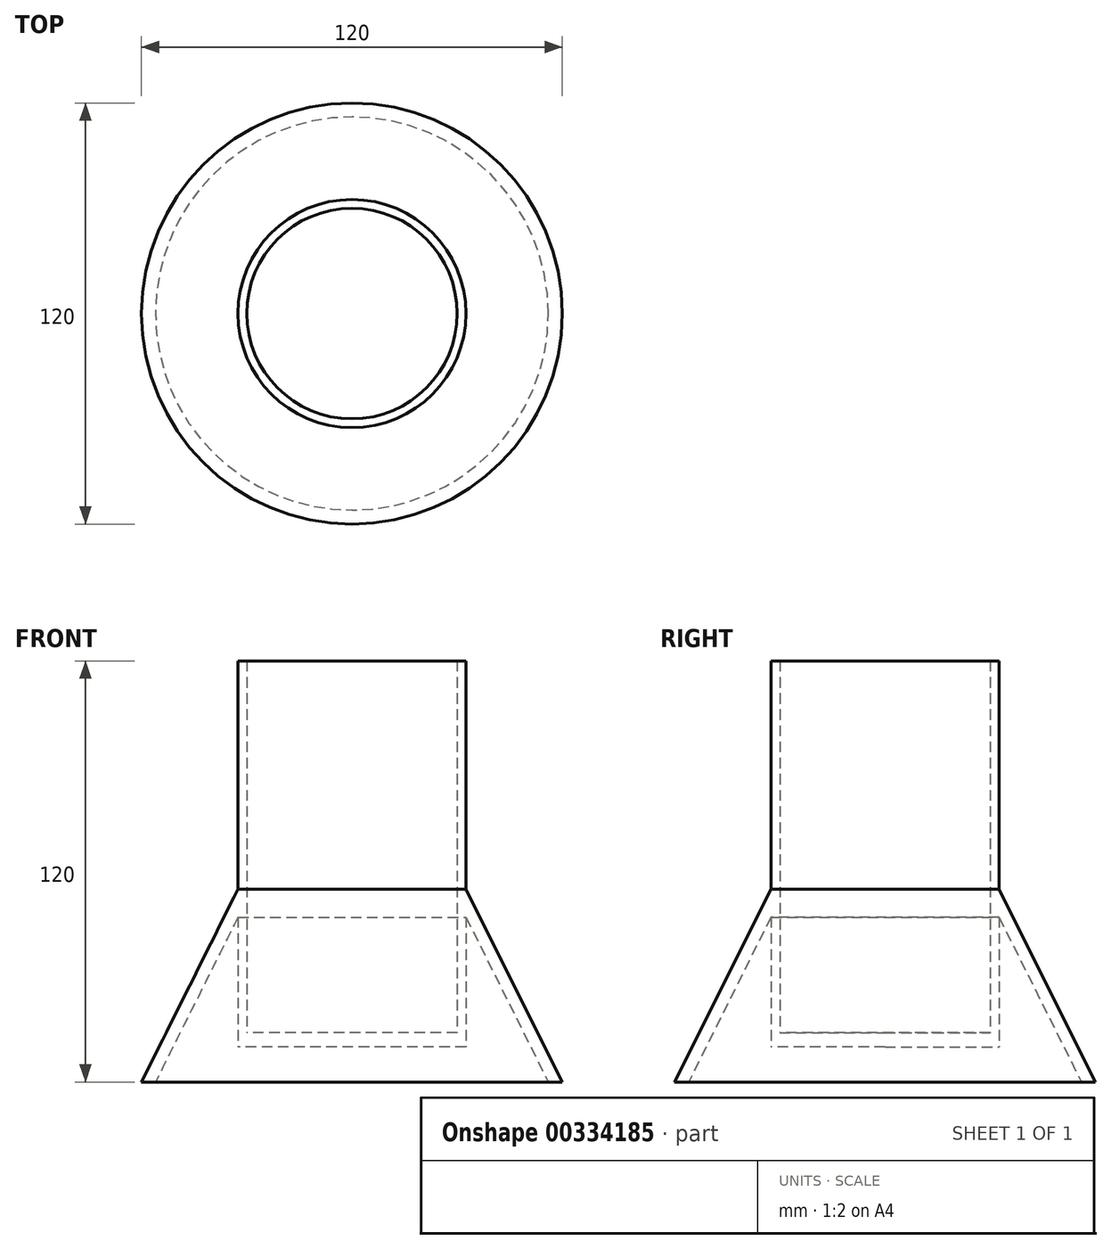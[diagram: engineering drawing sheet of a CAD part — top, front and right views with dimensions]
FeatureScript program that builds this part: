
annotation { "Feature Type Name" : "Feature", "Feature Type Description" : "" }
export const myFeature = defineFeature(function(context is Context, id is Id, definition is map)
    precondition{}
    {
        {
            var Q0;
            Q0=qCreatedBy(makeId("Top.planeOp"),FACE);
            var sketch = newSketch(context, id + "F0", { "sketchPlane" : qUnion([Q0])});
            skCircle(sketch, "E0", {"center": v(0, 0) * mm, "radius": 30 * mm});
            skCircle(sketch, "E1", {"center": v(0, 0) * mm, "radius": 32.5 * mm});
            skSolve(sketch);
        }
        {
            var Q0;
            Q0 = qSketchRegion(id + "F0", true);
            extrude(context, id + "F1", {"entities" : qUnion([Q0]), "depth" : 120 * mm});
        }
        {
            var Q0;
            Q0=qCreatedBy(makeId("Right.planeOp"),FACE);
            var sketch = newSketch(context, id + "F2", { "sketchPlane" : qUnion([Q0])});
            skLineSegment(sketch, "E2", {"start": v(-30, 0) * mm, "end": v(-30, 60) * mm});
            skLineSegment(sketch, "E3", {"start": v(-30, 60) * mm, "end": v(-60, 0) * mm});
            skLineSegment(sketch, "E4", {"start": v(-60, 0) * mm, "end": v(-56, 0) * mm});
            skLineSegment(sketch, "E5", {"start": v(-56, 0) * mm, "end": v(-30, 52) * mm});
            skLineSegment(sketch, "E6", {"start": v(0, 0) * mm, "end": v(0, 60) * mm});
            skSolve(sketch);
        }
        {
            var Q0;
            {var subQ0=sQuery(id+"F2.wireOp",EDGE,"E3");Q0=makeQuery(id+"F2.imprint","IMPRINT",FACE,{"disambiguationData":[TD([[makeQuery(id+"F2.imprint","IMPRINT",EDGE,{"derivedFrom":subQ0}),1.0]])]});}
            var Q1;
            Q1=sQuery(id+"F2.wireOp",EDGE,"E6");
            revolve(context, id + "F3", {"operationType" : NewBodyOperationType.ADD, "entities" : qUnion([Q0]), "axis" : qUnion([Q1]), "revolveType" : RevolveType.FULL});
        }
        {
            var Q0;
            Q0=makeQuery(id+"F1.opExtrude","CAP_FACE",FACE,{"disambiguationData":[OSD([sQuery(id+"F0.wireOp",EDGE,"E0"),sQuery(id+"F0.wireOp",EDGE,"E1")])],"isStart":true});
            extrude(context, id + "F4", {"entities" : qUnion([Q0]), "operationType" : NewBodyOperationType.REMOVE, "oppositeDirection" : true, "depth" : 10 * mm});
        }
        {
            var Q0;
            Q0=makeQuery(id+"F0.imprint","IMPRINT",FACE,{"disambiguationData":[TD([[makeQuery(id+"F0.imprint","IMPRINT",EDGE,{"derivedFrom":sQuery(id+"F0.wireOp",EDGE,"E0")}),1.0]])]});
            extrude(context, id + "F5", {"entities" : qUnion([Q0]), "operationType" : NewBodyOperationType.ADD, "depth" : 14 * mm});
        }
        {
            var Q0;
            Q0=makeQuery(id+"F5.opExtrude","CAP_FACE",FACE,{"disambiguationData":[OSD([sQuery(id+"F0.wireOp",EDGE,"E0")])],"isStart":true});
            extrude(context, id + "F6", {"entities" : qUnion([Q0]), "operationType" : NewBodyOperationType.REMOVE, "oppositeDirection" : true, "depth" : 10 * mm});
        }
    });
